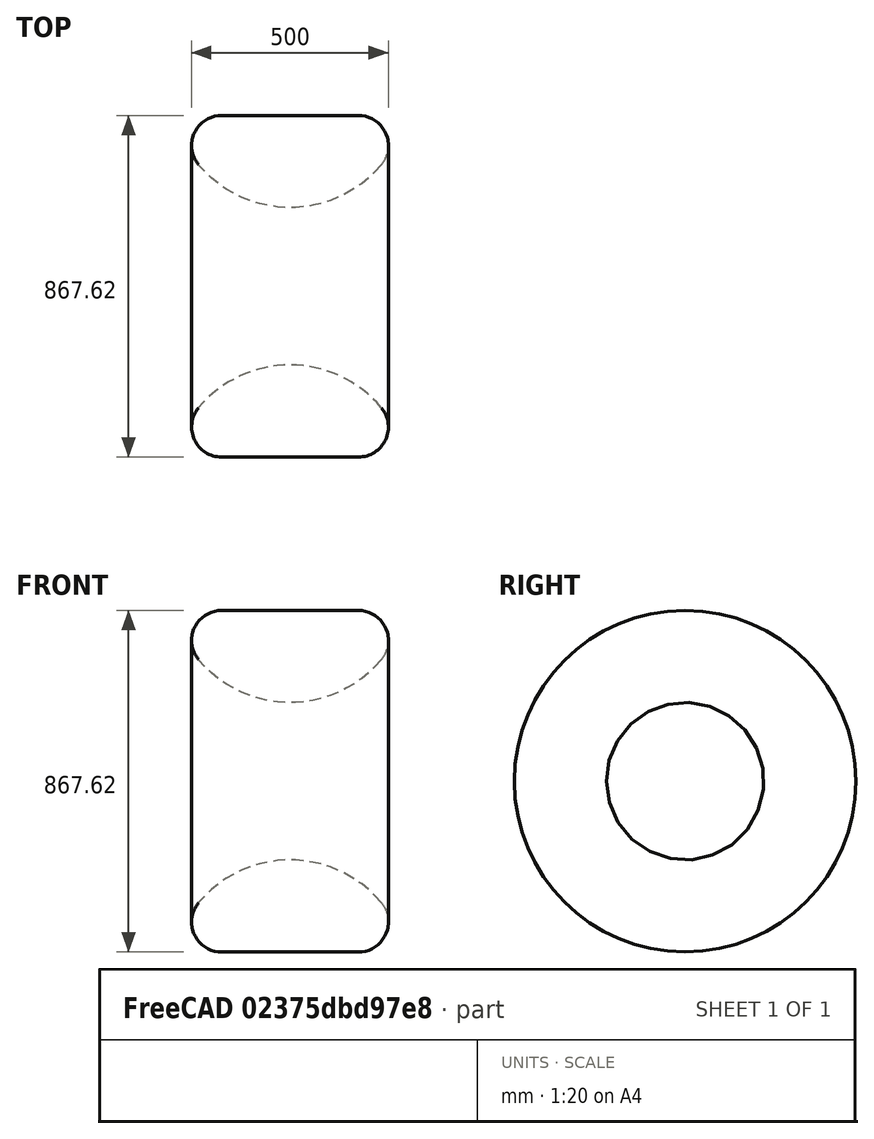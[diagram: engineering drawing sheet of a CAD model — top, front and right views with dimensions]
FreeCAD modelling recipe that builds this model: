
FCSTD DOCUMENT
Label: Profile0_rHWR1
objects: Sketcher::SketchObject×1, PartDesign::Revolution×1
note: 2 computed .brp shape members not serialized (recipe doc carries the construction recipe); baked Part::Feature solids carry a one-line shape summary decoded from their .brp

FEATURE [Sketcher::SketchObject] Sketch
  sketch-geometry (7):
    g0: LineSegment StartX=-222.482 StartY=-433.814 StartZ=0 EndX=125.518 EndY=-433.814 EndZ=0
    g1: ArcOfCircle CenterX=-222.482 CenterY=-357.814 CenterZ=0 NormalX=0 NormalY=0 NormalZ=1 Radius=76 StartAngle=2.44543 EndAngle=4.71239
    g2: ArcOfCircle CenterX=125.518 CenterY=-357.814 CenterZ=0 NormalX=0 NormalY=0 NormalZ=1 Radius=76 StartAngle=4.71239 EndAngle=6.97935
    g3: ArcOfCircle CenterX=-48.4819 CenterY=-501.931 CenterZ=0 NormalX=0 NormalY=0 NormalZ=1 Radius=301.931 StartAngle=0.696162 EndAngle=2.44543
    g4: LineSegment StartX=-280.797 StartY=-309.077 StartZ=0 EndX=-280.156 EndY=-308.309 EndZ=0
    g5: LineSegment StartX=183.192 StartY=-308.309 StartZ=0 EndX=183.834 EndY=-309.077 EndZ=0
    g6: LineSegment [constr] StartX=-156.794 StartY=-200 StartZ=0 EndX=101.679 EndY=-200 EndZ=0
  constraints (15):
    c: Horizontal(g0)
    c: Tangent(g1,g0)
    c: Tangent(g0,g2)
    c: Radius(g1) = 76
    c: Radius(g2) = 76
    c: Tangent(g3,g4)
    c: Tangent(g1,g4)
    c: Tangent(g3,g5)
    c: Tangent(g5,g2)
    c: Distance(g4) = 1
    c: Distance(g5) = 1
    c: Horizontal(g6)
    c: Tangent(g6,g3)
    c: DistanceY(g6) = -200
    c: Distance(g1,g2) = 348
FEATURE [PartDesign::Revolution] Revolution
  Angle = 360
  Axis = (1,0,0)
  Base = (0,0,0)
  Sketch = -> Sketch
